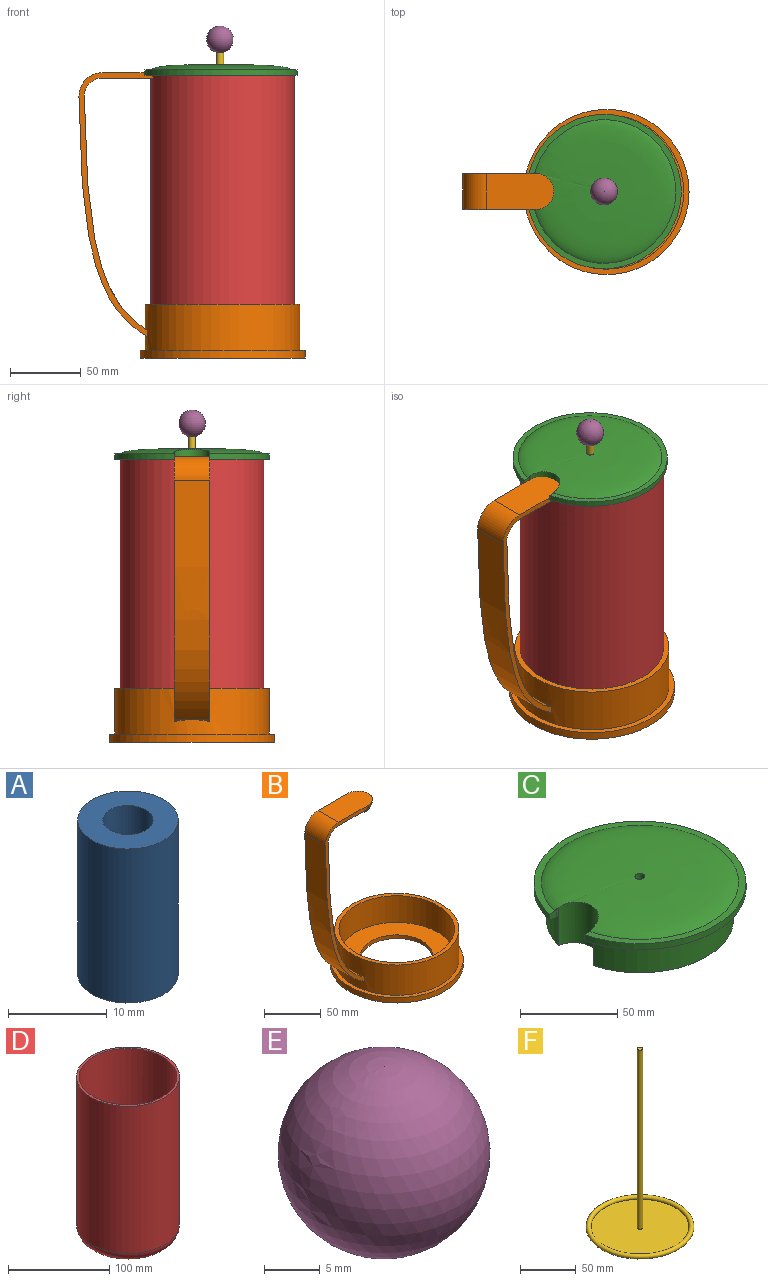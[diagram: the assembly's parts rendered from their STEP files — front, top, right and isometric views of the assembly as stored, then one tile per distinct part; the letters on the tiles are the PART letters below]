
ASSEMBLY  parts=6 mates=5
PART A: 4 faces, bbox 10.2x10.2x19.1 mm
  f0: cylinder r=2.54mm len=19.05mm, axis (0,0,-1), area 304mm2, adj f1,f3
  f1: plane 10.16x10.16mm, normal (0,0,1), area 60.8mm2, adj f0,f2
  f2: cylinder r=5.08mm len=19.05mm, axis (0,0,-1), area 608mm2, adj f1,f3
  f3: plane 10.16x10.16mm, normal (0,0,-1), area 60.8mm2, adj f0,f2
PART B: 28 faces, bbox 160.6x117.5x202.5 mm
  f0: plane 1.91x0.14mm, normal (1,0,0), area 0.1mm2, adj f3,f4,f25
  f1: plane 1.91x0.14mm, normal (1,0,0), area 0.1mm2, adj f2,f4,f25
  f2: plane 187.42x53.29mm, normal (0,-1,0), area 917.4mm2, adj f1,f5,f16,f17,f18,f19,f20,f21
  f3: plane 187.42x53.29mm, normal (0,1,0), area 917.4mm2, adj f0,f5,f15,f18,f19,f20,f21,f22
  f4: sphere r=12.7mm, area 479.7mm2, adj f0,f1,f21,f25,f26
  f5: cylinder r=54.61mm len=109.22mm, axis (0,0,1), area 11016.2mm2, adj f2,f3,f6,f14,f15,f16,f17,f24
  f6: plane 116.84x116.84mm, normal (0,0,1), area 1352.9mm2, adj f5,f7
  f7: cylinder r=58.42mm len=116.84mm, axis (0,0,1), area 2071.2mm2, adj f6,f8
  f8: plane 116.84x116.84mm, normal (0,0,-1), area 2614.6mm2, adj f7,f9
  f9: cylinder r=50.8mm len=101.6mm, axis (0,0,1), area 1801.1mm2, adj f8,f10
  f10: plane 101.6x101.6mm, normal (0,0,-1), area 4940.4mm2, adj f9,f11
  f11: cylinder r=31.75mm len=63.5mm, axis (0,0,1), area 760.1mm2, adj f10,f12
  f12: plane 101.6x101.6mm, normal (0,0,1), area 4940.4mm2, adj f11,f13
  f13: cylinder r=50.8mm len=101.6mm, axis (0,0,1), area 9143.8mm2, adj f12,f14
  f14: plane 109.22x109.22mm, normal (0,0,1), area 1261.7mm2, adj f5,f13
  f15: plane 13.27x2.07mm, normal (0.61,0,0.79), area 7.9mm2, adj f3,f5,f18
  f16: plane 13.36x2.16mm, normal (-0.66,0,-0.75), area 8.4mm2, adj f2,f5,f23
  f17: plane 13.27x2.07mm, normal (0.61,0,0.79), area 7.9mm2, adj f2,f5,f18
  f18: extruded ~164.86x43.13mm, area 4488mm2, adj f2,f3,f15,f17,f19
  f19: cylinder r=12.7mm len=25.4mm, axis (0,1,0), area 509.4mm2, adj f2,f3,f18,f20
  f20: plane 35.85x25.4mm, normal (0,0,-1), area 883.2mm2, adj f2,f3,f19,f27
  f21: plane 49.48x25.4mm, normal (0,0,1), area 1187.5mm2, adj f2,f3,f4,f22
  f22: cylinder r=16.65mm len=25.4mm, axis (0,1,0), area 659.9mm2, adj f2,f3,f21,f23
  f23: extruded ~169.47x46.94mm, area 4648.1mm2, adj f2,f3,f16,f22,f24
  f24: plane 13.36x2.16mm, normal (-0.66,0,-0.75), area 8.4mm2, adj f3,f5,f23
  f25: plane 25.4x4.17mm, normal (0,0,-1), area 64.6mm2, adj f0,f1,f2,f3,f4,f26,f27
  f26: cylinder r=48.26mm len=24.9mm, axis (0,0,1), area 135.9mm2, adj f4,f25
  f27: cylinder r=50.8mm len=25.4mm, axis (0,0,1), area 48.9mm2, adj f2,f3,f20,f25
PART C: 18 faces, bbox 107.8x109.3x26.8 mm
  f0: plane 91.44x89.09mm, normal (0,0,-1), area 6219.2mm2, adj f9,f10,f13
  f1: cylinder r=54.61mm len=109.22mm, axis (0,0,-1), area 1209.6mm2, adj f2,f6,f8,f15
  f2: plane 4.91x4.44mm, normal (0,-1,0), area 18.8mm2, adj f1,f3,f8,f15,f17
  f3: plane 5.19x1.79mm, normal (-0.07,-1,0), area 8mm2, adj f2,f4,f8,f17
  f4: cylinder r=12.69mm len=25.95mm, axis (0,0,-1), area 934.3mm2, adj f3,f5,f11,f12,f16
  f5: plane 5.19x1.79mm, normal (-0.07,1,0), area 8mm2, adj f4,f6,f8,f16
  f6: plane 4.91x4.44mm, normal (0,1,0), area 18.8mm2, adj f1,f5,f8,f15,f16
  f7: cylinder r=2.54mm len=26.67mm, axis (0,0,-1), area 425.6mm2, adj f14,f16
  f8: plane 109.22x107.72mm, normal (0,0,-1), area 1889.4mm2, adj f1,f2,f3,f5,f6,f11
  f9: cylinder r=45.72mm len=91.44mm, axis (0,0,1), area 4912mm2, adj f0,f10,f12
  f10: cylinder r=15.23mm len=28.92mm, axis (0,0,1), area 726.2mm2, adj f0,f9,f12
  f11: cylinder r=48.26mm len=96.52mm, axis (0,0,1), area 5291.2mm2, adj f4,f8,f12
  f12: plane 96.52x94.85mm, normal (0,0,-1), area 775.1mm2, adj f4,f9,f10,f11
  f13: cylinder r=5.08mm len=19.05mm, axis (0,0,1), area 608mm2, adj f0,f14
  f14: plane 10.16x10.16mm, normal (0,0,-1), area 60.8mm2, adj f7,f13
  f15: plane 109.22x107.72mm, normal (0,0,1), area 1164mm2, adj f1,f2,f6,f16,f17
  f16: revolved ~100.76x100.76mm, area 7911.8mm2, adj f4,f5,f6,f7,f15,f17
  f17: revolved ~2.6x1.26mm, area 0.8mm2, adj f2,f3,f15,f16
PART D: 7 faces, bbox 110x110x190.5 mm
  f0: plane 101.6x101.6mm, normal (0,0,1), area 790.5mm2, adj f1,f4
  f1: cylinder r=50.8mm len=177.8mm, axis (0,0,1), area 56751.2mm2, adj f0,f2
  f2: torus R=38.1mm, axis (0,0,1), area 5789mm2, adj f1,f3
  f3: plane 76.2x76.2mm, normal (0,0,-1), area 4560.4mm2, adj f2
  f4: cylinder r=48.26mm len=177.8mm, axis (0,0,1), area 53913.7mm2, adj f0,f5
  f5: torus R=38.1mm, axis (0,0,1), area 4469.1mm2, adj f4,f6
  f6: plane 76.2x76.2mm, normal (0,0,1), area 4560.4mm2, adj f5
PART E: 3 faces, bbox 19.1x19.1x18.7 mm
  f0: cylinder r=2.54mm len=9.18mm, axis (0,0,-1), area 146.5mm2, adj f1,f2
  f1: plane 5.08x5.08mm, normal (0,0,-1), area 20.3mm2, adj f0
  f2: sphere r=9.53mm, area 1119.4mm2, adj f0
PART F: 5 faces, bbox 105x105x198.1 mm
  f0: torus R=46.23mm, axis (0,0,-1), area 3406.1mm2, adj f1,f4
  f1: plane 92.46x92.46mm, normal (0,0,-1), area 6714.1mm2, adj f0
  f2: plane 5.08x5.08mm, normal (0,0,1), area 20.3mm2, adj f3
  f3: cylinder r=2.54mm len=196.85mm, axis (0,0,-1), area 3141.6mm2, adj f2,f4
  f4: plane 88.4x88.4mm, normal (0,0,1), area 6117mm2, adj f0,f3
PLACE A t=(19.85,-0.2,-66.05)mm
PLACE B t=(21.56,-0.2,0.62)mm
PLACE C t=(19.85,-0.2,0.62)mm
PLACE D t=(21.56,-0.2,0.62)mm fixed
PLACE E t=(19.85,-0.2,-66.05)mm
PLACE F t=(19.85,-0.2,-66.05)mm
MATE slider A.f0 <-> C.f11  axis (0,0,1) through (19.85,-0.2,-56.53)mm
MATE fastened E.f0 <-> F.f0  axis (0,0,1) through (19.85,-0.2,121.27)mm
MATE fastened D.f2 <-> B.f5  axis (0,0,-1) through (21.56,-0.2,-94.63)mm
MATE slider C.f0 <-> D.f2  axis (0,0,-1) through (21.56,-0.2,95.87)mm
MATE fastened A.f0 <-> F.f0  axis (0,0,-1) through (19.85,-0.2,-75.58)mm
